# Revit family: KDW010054
name_source: partatom
category: Plumbing Fixtures
revit_build: Autodesk Revit 2015 (Build: 20140606_1530(x64)
units: mm (PartAtom-declared; Revit-internal decimal feet)

## types (1)
- KDW010054
    BIMobject category = Bath & Spas
    Brand url = http://www.kaldewei.com
    Color = https://www.kaldewei.co.uk
    ColourOptions = https://www.kaldewei.co.uk
    ConnectingDimensions = EN 232
    Design country = Germany
    DrainSize = 52 mm
    Durability = https://www.kaldewei.de
    Edition number = 1
    Features = https://www.kaldewei.co.uk
    Finish = https://www.kaldewei.co.uk
    Finition = Kaldewei
    HasGrabHandles = https://www.kaldewei.co.uk
    IFC Classification = Furnishing Element
    IfcExportAs = BATH
    IfcExportType = IfcSanitaryTerminalType
    IntegralAccessories = https://www.kaldewei.co.uk
    Manufacturer = Kaldewei
    Manufacturer country = Germany
    ManufacturerCountry = GERMANY
    ManufacturerName = KALDEWEI
    ManufacturerURL = https://www.kaldewei.com
    Material = steel enamel
    Material main = Steel
    Material secondary = Enamel
    Model = ASYMMETRIC DUO
    NBS Reference Code = 35-06-08
    NBS Reference Description = Baths
    Name = ASYMMETRICDUO
    Nominal height = 800 cm
    Nominal width = 1700 cm
    NominalDepth = 425
    NominalLength = 1700
    ObjectName = ASYMMETRICDUO 800x1700x425
    ObjectNorm = EN 14516EU DECLARATION OF PERFORMANCE(https://www.kaldewei.de
    ObjectPicture = https://www.kaldewei.co.uk
    ObjectURL = https://www.kaldewei.co.uk
    Polantis code = KDW010054
    Product Guid = a03c7cdf-5c67-49f0-9ef0-5e3adb6818b1
    Product SKU = 740
    Product certification = https://www.kaldewei.co.uk
    Product data url = https://bimobject.com
    Product family = ASYMMETRIC DUO
    Product group = Bathtub
    Product url = https://www.kaldewei.co.uk
    ProductInformation = Model No.740: A bath with a comfort zone: with its generously proportioned storage shelf, the ASYMMETRIC DUO also has a spatial dimension. It can be used as a seat or for holding bath utensils, and also for the individual positioning of taps.There is a charming contrast between the precise and clear form of the bath rim and the ergonomic, flowing design language of the inside. Furthermore, the outflow set flush into the base of the bath is an elegant and harmonious solution.
    QR code = http://bimobject.com
    Revision = 1
    SerialNumber = 740
    Shape = Rectangular baths
    Size = 800x1700x425
    SupportFrame = https://www.kaldewei.co.uk
    Sustainability = https://kaldewei-fa.secure.footprint.net
    Technical description = https://www.kaldewei.co.uk
    TechnicalDataURL = https://kaldewei.typo-live.web-factory.de
    Type Comments = ASYMMETRIC DUO 740 800x1700x425
    UNSPSC Code = 30181501
    UNSPSCCode = 30181500
    UNSPSCNames = Sanitary ware
    URL = https://www.kaldewei.co.uk
    Uniclass 1.4 Code = L7211
    Uniclass 1.4 Description = Baths
    Uniclass 2.0 Code = PR-35-06-08
    Uniclass 2.0 Description = Baths
    Uniclass 2015 = Pr_40_20_06_08
    Version = 5
    VolumeToOverflowMaximum = 123
    WarrantyDurationParts = 30
    WarrantyDurationUnit = Year
    WarrantyStartDate = https://www.kaldewei.co.uk
    WaterSupplyOverflowAndWasteHolesOverflow = 52 mm
    WaterSupplyOverflowAndWasteHolesWaste = 52 mm
    Weight = 50
    Weight Net (Kg) = 50

## geometry (parser evidence)
native form markers: Sweep x2
no freeform markers — native parametric forms only
